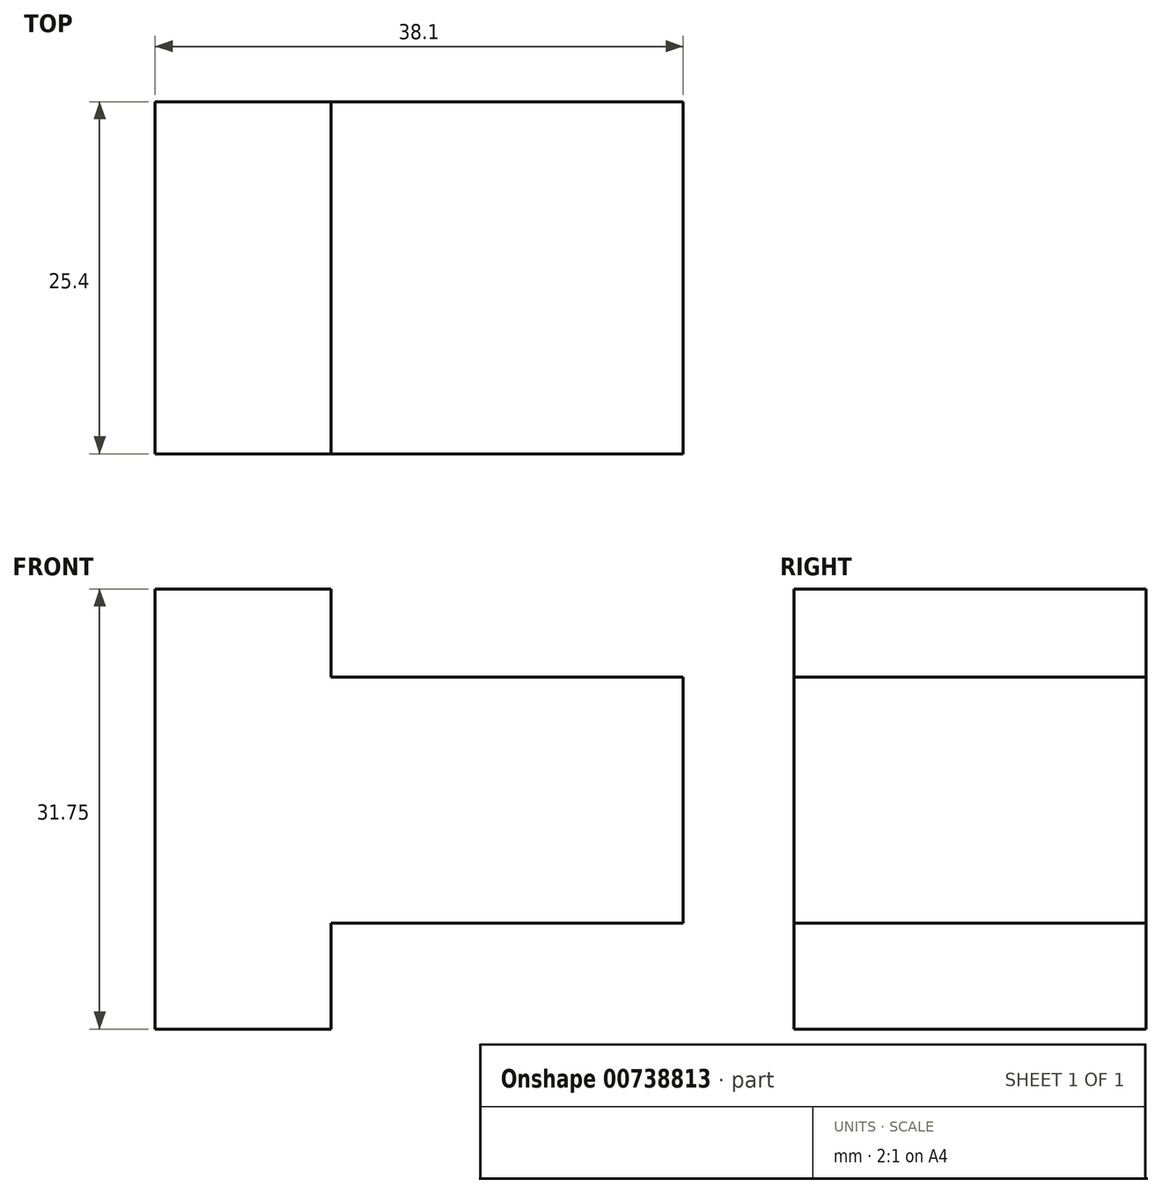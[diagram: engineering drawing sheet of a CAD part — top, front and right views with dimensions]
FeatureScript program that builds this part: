
annotation { "Feature Type Name" : "Feature", "Feature Type Description" : "" }
export const myFeature = defineFeature(function(context is Context, id is Id, definition is map)
    precondition{}
    {
        {
            var Q0;
            Q0=qCreatedBy(makeId("Front.planeOp"),FACE);
            var sketch = newSketch(context, id + "F0", { "sketchPlane" : qUnion([Q0])});
            skLineSegment(sketch, "E0", {"start": v(0, 0) * mm, "end": v(0, 31.75) * mm});
            skLineSegment(sketch, "E1", {"start": v(0, 31.75) * mm, "end": v(38.1, 31.75) * mm});
            skLineSegment(sketch, "E2", {"start": v(38.1, 31.75) * mm, "end": v(38.1, 0) * mm});
            skLineSegment(sketch, "E3", {"start": v(38.1, 0) * mm, "end": v(0, 0) * mm});
            skSolve(sketch);
        }
        {
            var Q0;
            Q0 = qSketchRegion(id + "F0", true);
            extrude(context, id + "F1", {"entities" : qUnion([Q0]), "depth" : 25.4 * mm, "offsetDistance" : 25.4 * mm});
        }
        {
            var Q0;
            Q0=makeQuery(id+"F1.opExtrude","CAP_FACE",FACE,{"disambiguationData":[OSD([sQuery(id+"F0.wireOp",EDGE,"E0"),sQuery(id+"F0.wireOp",EDGE,"E1"),sQuery(id+"F0.wireOp",EDGE,"E2"),sQuery(id+"F0.wireOp",EDGE,"E3")])],"isStart":false});
            var sketch = newSketch(context, id + "F2", { "sketchPlane" : qUnion([Q0])});
            skLineSegment(sketch, "E4", {"start": v(12.7, 31.75) * mm, "end": v(12.7, 25.4) * mm});
            skLineSegment(sketch, "E5", {"start": v(12.7, 25.4) * mm, "end": v(38.1, 25.4) * mm});
            skLineSegment(sketch, "E6", {"start": v(12.7, 0) * mm, "end": v(12.7, 7.63) * mm});
            skLineSegment(sketch, "E7", {"start": v(12.7, 7.63) * mm, "end": v(38.1, 7.63) * mm});
            skSolve(sketch);
        }
        {
            var Q0;
            {var subQ0=sQuery(id+"F2.wireOp",EDGE,"E4");Q0=makeQuery(id+"F2.imprint","IMPRINT",FACE,{"disambiguationData":[TD([[makeQuery(id+"F2.imprint","IMPRINT",EDGE,{"derivedFrom":subQ0}),1.0]])]});}
            var Q1;
            {var subQ0=sQuery(id+"F2.wireOp",EDGE,"E6");Q1=makeQuery(id+"F2.imprint","IMPRINT",FACE,{"disambiguationData":[TD([[makeQuery(id+"F2.imprint","IMPRINT",EDGE,{"derivedFrom":subQ0}),-1.0]])]});}
            extrude(context, id + "F3", {"entities" : qUnion([Q0, Q1]), "operationType" : NewBodyOperationType.REMOVE, "endBound" : BoundingType.THROUGH_ALL, "oppositeDirection" : true, "depth" : 25.4 * mm, "offsetDistance" : 25.4 * mm});
        }
    });
